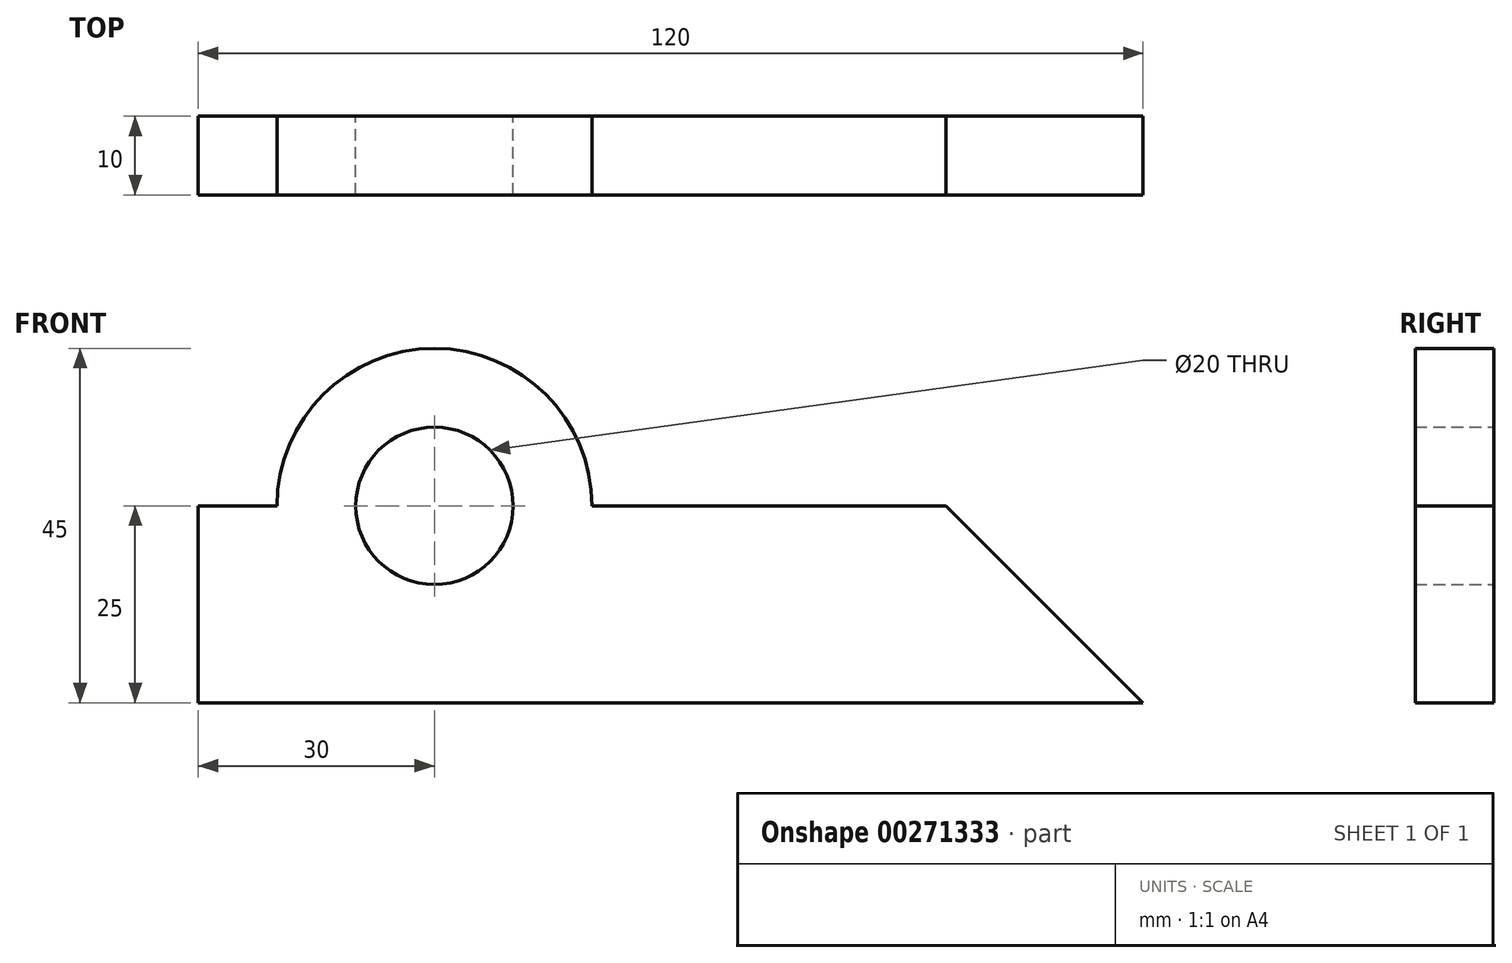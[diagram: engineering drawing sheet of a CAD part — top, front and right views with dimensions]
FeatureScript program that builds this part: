
annotation { "Feature Type Name" : "Feature", "Feature Type Description" : "" }
export const myFeature = defineFeature(function(context is Context, id is Id, definition is map)
    precondition{}
    {
        {
            var Q0;
            Q0=qCreatedBy(makeId("Front.planeOp"),FACE);
            var sketch = newSketch(context, id + "F0", { "sketchPlane" : qUnion([Q0])});
            skLineSegment(sketch, "E0", {"start": v(0, 0) * mm, "end": v(120, 0) * mm});
            skLineSegment(sketch, "E1", {"start": v(0, 0) * mm, "end": v(0, 25) * mm});
            skLineSegment(sketch, "E2", {"start": v(120, 0) * mm, "end": v(95, 25) * mm});
            skCircle(sketch, "E3", {"center": v(30, 25) * mm, "radius": 10 * mm});
            skLineSegment(sketch, "E4", {"start": v(0, 25) * mm, "end": v(10, 25) * mm});
            skArc(sketch, "E5", {"start": v(50, 25) * mm, "mid": v(30, 45) * mm, "end": v(10, 25) * mm});
            skLineSegment(sketch, "E6", {"start": v(50, 25) * mm, "end": v(95, 25) * mm});
            skSolve(sketch);
        }
        {
            var Q0;
            Q0=makeQuery(id+"F0.imprint","IMPRINT",FACE,{"disambiguationData":[TD([[makeQuery(id+"F0.imprint","IMPRINT",EDGE,{"derivedFrom":sQuery(id+"F0.wireOp",EDGE,"E0")}),1.0]])]});
            extrude(context, id + "F1", {"entities" : qUnion([Q0]), "depth" : 10 * mm});
        }
    });
